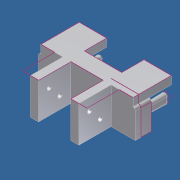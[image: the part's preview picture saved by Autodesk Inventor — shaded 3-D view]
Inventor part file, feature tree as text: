
AUTODESK INVENTOR PART (.ipt)
format: ipt  version: unknown  size: 402,432 bytes
history: native  units: in
note: dims shown in document units (in); Inventor stores cm internally (conversion verified against a paired STEP export)
features: other x20, sketch x16, extrude x12, fillet x1, mirror x1
ambient origin geometry x8: Origin, YZ Plane, XZ Plane, XY Plane, X Axis, Y Axis, Z Axis, Center Point
bodies: Solid2 (feature_tree)
feature tree (50):
  sketch  "Sketch1"  dims[d15=0.1437in d18=0.69in d19=-0.0069in]
  extrude  "Extrusion2"  Depth=0.69in
  extrude  "Extrusion3"  Depth=0.25in
  extrude  "Extrusion4"  Depth=0.06in
  sketch  "Sketch4"  dims[d35=0.174in d36=0.0in d37=0.25in d38=0.0in]
  fillet  "Fillet1"  Radius=0.076in
  extrude  "Extrusion5"  Depth=0.25in TaperAngle=0.0deg
  sketch  "Sketch7"  dims[d42=1.0in d43=0.0in d44=0.25in]
  sketch  "Sketch8"  dims[d45=1.0in d46=0.0in d52=0.14in]
  extrude  "Extrusion6"  Depth=0.25in
  extrude  "Extrusion7"  Depth=0.25in
  extrude  "Extrusion8"  Depth=0.14in
  extrude  "Extrusion9"  Depth=1.0in TaperAngle=0.0deg
  extrude  "Extrusion10"  Depth=0.5in TaperAngle=0.0deg
  extrude  "Extrusion11"  [1 undecoded]
  extrude  "Extrusion12"  [1 undecoded]
  mirror  "Mirror1"
  sketch  "Sketch17"
  extrude  "Extrusion13"  [1 undecoded]
  sketch  "Sketch2"  dims[d25=0.25in d26=0.0in d27=0.25in]
  sketch  "Sketch3"  dims[d28=0.94in d29=0.0in d30=0.06in d31=0.076in d32=0.0in]
  sketch  "Sketch5"  dims[d39=0.25in d40=0.0in d41=0.25in]
  sketch  "Sketch9"  dims[d53=0.14in d54=1.0in d55=0.0in]
  sketch  "Sketch10"  dims[d56=0.5in d57=0.5in d58=0.0in]
  sketch  "Sketch11"  dims[d59=2.0in d60=0.0in]
  sketch  "Sketch12"
  sketch  "Sketch13"
  sketch  "Sketch14"
  sketch  "Sketch16"
  sketch  "Sketch18"
  other  "Composite1"
  other  "Composite2"
  other  "Composite3"
  other  "Composite4"
  other  "Composite5"
  other  "Composite6"
  other  "Composite7"
  other  "Composite8"
  other  "Composite9"
  other  "Composite10"
  other  "Srf1"
  other  "Srf2"
  other  "Srf3"
  other  "Srf4"
  other  "Srf5"
  other  "Srf6"
  other  "Srf7"
  other  "Srf8"
  other  "Srf9"
  other  "Srf10"
note: 3 required parameter values undecoded (feature->parameter linkage not recoverable at this tier; creation-order binding heuristic only, values carry confidence <= 0.55)
